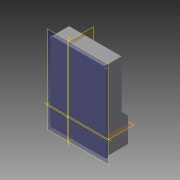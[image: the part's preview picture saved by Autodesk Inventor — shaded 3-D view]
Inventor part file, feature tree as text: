
AUTODESK INVENTOR PART (.ipt)
format: ipt  version: 2015 (Build 190159000, 159)  size: 167,424 bytes
history: native  units: mm
features: extrude x7, sketch x7, projected_geometry x4
ambient origin geometry x8: Origin, YZ Plane, XZ Plane, XY Plane, X Axis, Y Axis, Z Axis, Center Point
bodies: Solid1 (feature_tree)
feature tree (18):
  extrude  "Extrusion1"  Depth=96.5mm
  extrude  "Extrusion2"  TaperAngle=0.0deg  [1 undecoded]
  extrude  "Extrusion3"  Depth=2.0mm
  extrude  "Extrusion4"  Depth=2.0mm
  extrude  "Extrusion5"  Depth=2.0mm
  extrude  "Extrusion6"  Depth=2.0mm TaperAngle=0.0deg
  extrude  "Extrusion7"  Depth=2.0mm
  sketch  "Sketch1"  dims[d0=68.0mm d1=96.5mm]
  sketch  "Sketch3"  dims[d2=2.0mm d3=0.0mm d4=0.0mm]
  projected_geometry  "Projected Loop1"
  sketch  "Sketch4"  dims[d5=2.0mm d7=2.0mm]
  projected_geometry  "Projected Loop2"
  sketch  "Sketch5"  dims[d8=0.0mm d9=2.0mm]
  projected_geometry  "Projected Loop3"
  projected_geometry  "Projected Loop4"
  sketch  "Sketch6"  dims[d10=2.0mm d11=2.0mm]
  sketch  "Sketch7"  dims[d12=25.0mm d13=0.0mm d14=2.0mm d15=0.0mm]
  sketch  "Sketch13"  dims[d16=2.0mm d17=2.0mm d18=2.0mm d19=0.0mm d20=27.0mm d21=10.0mm d22=45.0deg d23=2.0mm d24=0.0mm d25=2.0mm d26=2.0mm d27=0.0mm d46=10.0mm d47=15.0mm d48=2.0mm d49=0.0mm]
note: 1 required parameter value undecoded (feature->parameter linkage not recoverable at this tier; creation-order binding heuristic only, values carry confidence <= 0.55)
